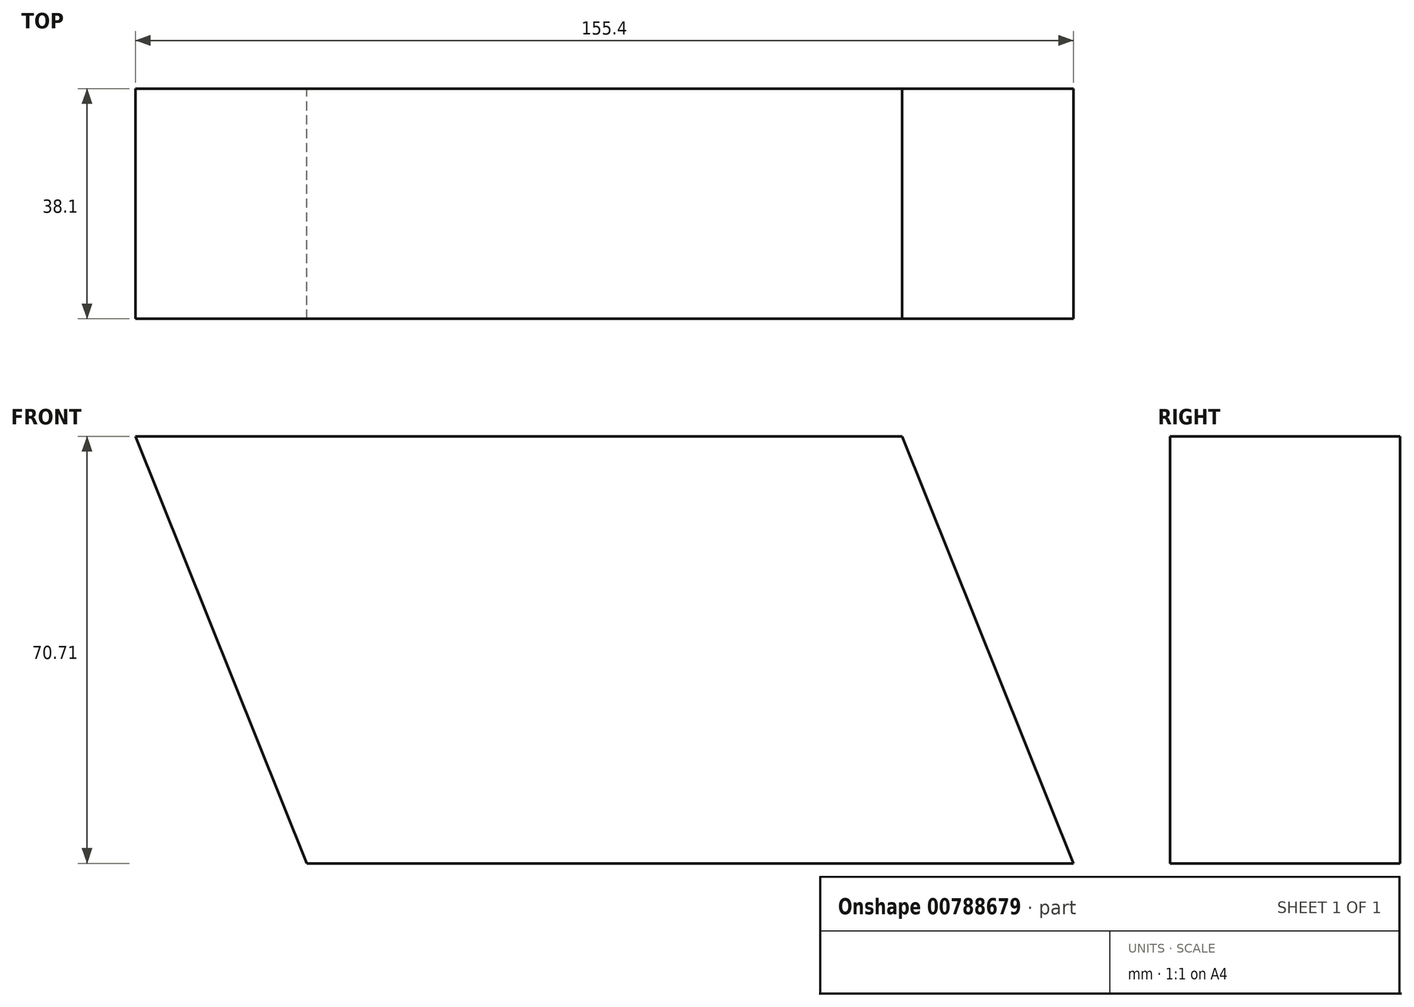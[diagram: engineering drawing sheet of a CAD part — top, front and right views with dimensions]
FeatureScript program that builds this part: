
annotation { "Feature Type Name" : "Feature", "Feature Type Description" : "" }
export const myFeature = defineFeature(function(context is Context, id is Id, definition is map)
    precondition{}
    {
        {
            var Q0;
            Q0=qCreatedBy(makeId("Front.planeOp"),FACE);
            var sketch = newSketch(context, id + "F0", { "sketchPlane" : qUnion([Q0])});
            skLineSegment(sketch, "E0", {"start": v(50.41, -19.8) * mm, "end": v(22.01, 50.9) * mm});
            skLineSegment(sketch, "E1", {"start": v(22.01, 50.9) * mm, "end": v(-104.99, 50.9) * mm});
            skLineSegment(sketch, "E2", {"start": v(-104.99, 50.9) * mm, "end": v(-76.59, -19.8) * mm});
            skLineSegment(sketch, "E3", {"start": v(-76.59, -19.8) * mm, "end": v(50.41, -19.8) * mm});
            skSolve(sketch);
        }
        {
            var Q0;
            Q0 = qSketchRegion(id + "F0", true);
            extrude(context, id + "F1", {"entities" : qUnion([Q0]), "depth" : 38.1 * mm, "offsetDistance" : 25.4 * mm});
        }
    });
